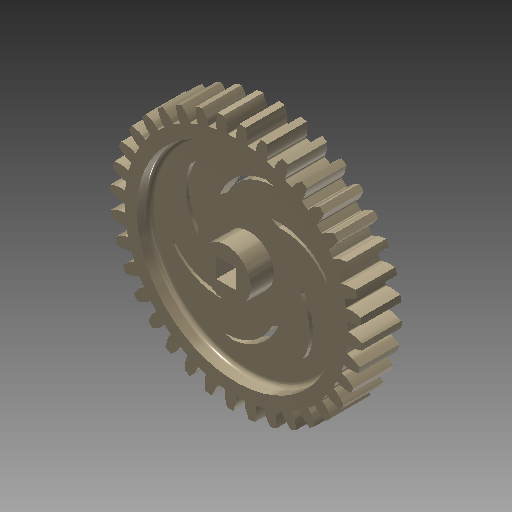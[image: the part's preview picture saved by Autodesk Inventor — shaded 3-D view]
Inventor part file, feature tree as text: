
AUTODESK INVENTOR PART (.ipt)
format: ipt  version: 2018 (Build 220112000, 112)  size: 1,144,320 bytes
history: native  units: mm (DEFAULTED — no unit token found)
features: imported_body x1, sketch x1, other x1, extrude x1
ambient origin geometry x8: Origin, YZ Plane, XZ Plane, XY Plane, X Axis, Y Axis, Z Axis, Center Point
bodies: Solid1 (feature_tree)
feature tree (4):
  imported_body  "Base1"
  sketch  "Sketch1"  dims[d0=25.4mm d1=0.0mm d2=0.0mm d3=0.0mm]
  other  "Srf1"
  extrude  "ExtrusionSrf1"  TaperAngle=0.0deg  [1 undecoded]
note: 1 required parameter value undecoded (feature->parameter linkage not recoverable at this tier; creation-order binding heuristic only, values carry confidence <= 0.55)
